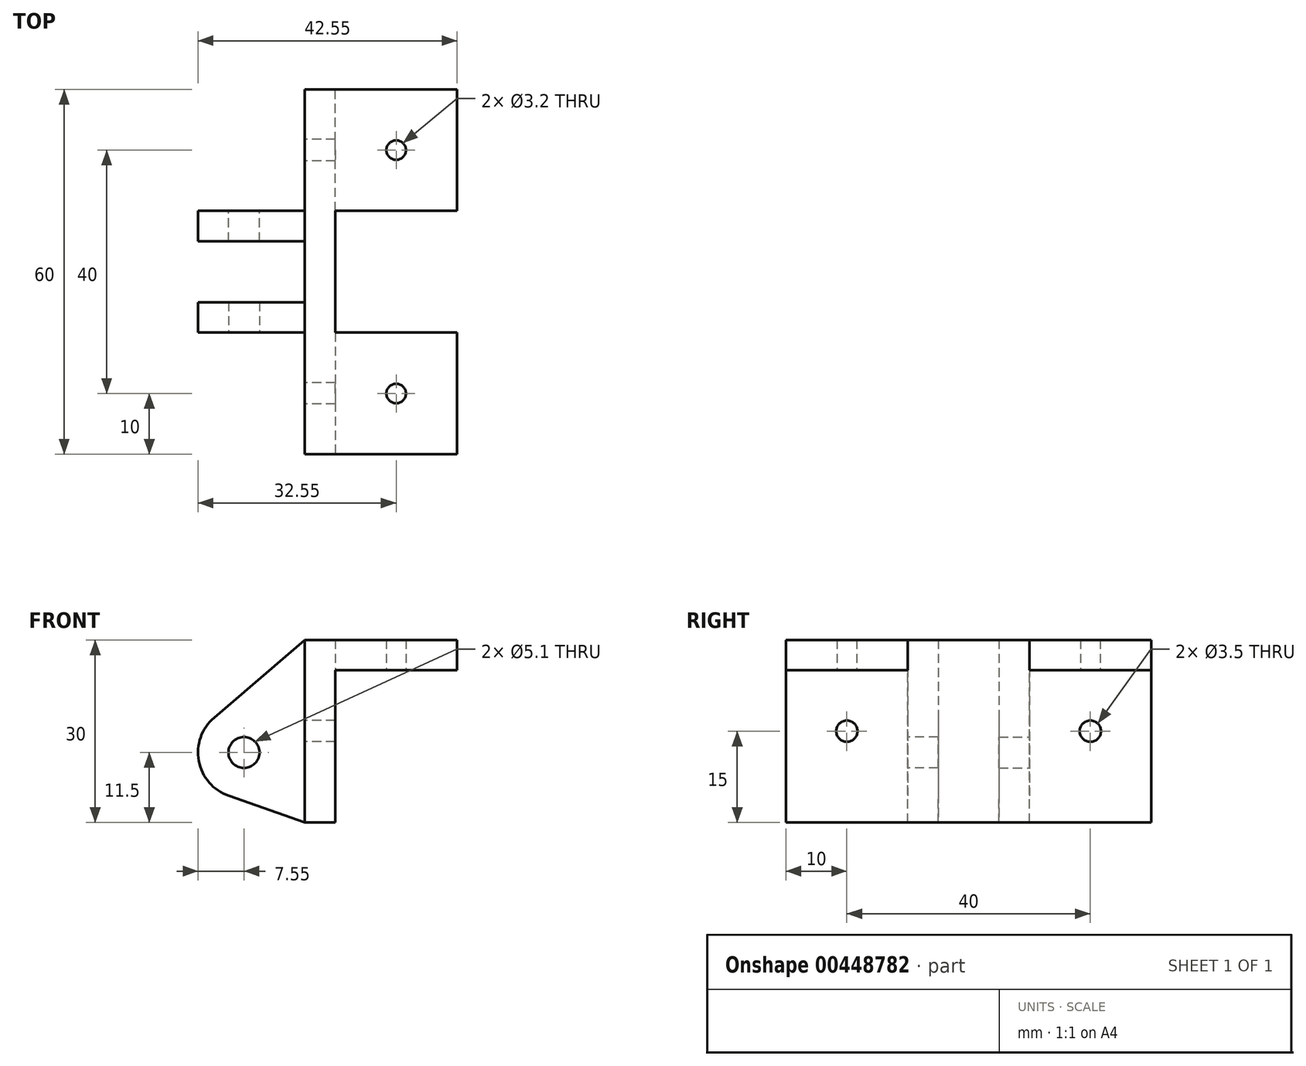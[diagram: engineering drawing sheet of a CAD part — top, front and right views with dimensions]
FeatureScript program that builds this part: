
annotation { "Feature Type Name" : "Feature", "Feature Type Description" : "" }
export const myFeature = defineFeature(function(context is Context, id is Id, definition is map)
    precondition{}
    {
        {
            var Q0;
            Q0=qCreatedBy(makeId("Front.planeOp"),FACE);
            var sketch = newSketch(context, id + "F0", { "sketchPlane" : qUnion([Q0])});
            skLineSegment(sketch, "E0", {"start": v(25, 0) * mm, "end": v(0, 0) * mm});
            skLineSegment(sketch, "E1", {"start": v(0, 0) * mm, "end": v(0, 30) * mm});
            skLineSegment(sketch, "E2", {"start": v(0, 30) * mm, "end": v(25, 30) * mm});
            skLineSegment(sketch, "E3", {"start": v(25, 30) * mm, "end": v(25, 25) * mm});
            skLineSegment(sketch, "E4", {"start": v(25, 25) * mm, "end": v(5, 25) * mm});
            skLineSegment(sketch, "E5", {"start": v(5, 25) * mm, "end": v(5, 5) * mm});
            skLineSegment(sketch, "E6", {"start": v(5, 5) * mm, "end": v(25, 5) * mm});
            skLineSegment(sketch, "E7", {"start": v(25, 5) * mm, "end": v(25, 0) * mm});
            skSolve(sketch);
        }
        {
            var Q0;
            Q0=qSketchRegion(id+"F0",true);
            extrude(context, id + "F1", {"entities" : qUnion([Q0]), "depth" : 20 * mm});
        }
        {
            var Q0;
            Q0=makeQuery(id+"F1.opExtrude","SWEPT_FACE",FACE,{"disambiguationData":[OSD([sQuery(id+"F0.wireOp",EDGE,"E4")])]});
            var sketch = newSketch(context, id + "F2", { "sketchPlane" : qUnion([Q0])});
            skPoint(sketch, "E8", {"position": v(15, 10) * mm});
            skPoint(sketch, "E8.positionSnap0", {"position": v(25, 10) * mm});
            skPoint(sketch, "E8.positionSnap1", {"position": v(15, 20) * mm});
            skSolve(sketch);
        }
        {
            var Q0;
            Q0=makeQuery(id+"F1.opExtrude","SWEPT_FACE",FACE,{"disambiguationData":[OSD([sQuery(id+"F0.wireOp",EDGE,"E6")])]});
            var sketch = newSketch(context, id + "F3", { "sketchPlane" : qUnion([Q0])});
            skPoint(sketch, "E9", {"position": v(15, -10) * mm});
            skPoint(sketch, "E9.positionSnap0", {"position": v(25, -10) * mm});
            skPoint(sketch, "E9.positionSnap1", {"position": v(15, -20) * mm});
            skSolve(sketch);
        }
        {
            var Q0;
            Q0=sQuery(id+"F2.wireOp",VERTEX,"E8");
            var Q1;
            Q1=sQuery(id+"F3.wireOp",VERTEX,"E9");
            var Q2;
            Q2=makeQuery(id+"F1.opExtrude","SWEPT_BODY",BODY,{"disambiguationData":[OSD([sQuery(id+"F0.wireOp",EDGE,"E0"),sQuery(id+"F0.wireOp",EDGE,"E1"),sQuery(id+"F0.wireOp",EDGE,"E2"),sQuery(id+"F0.wireOp",EDGE,"E3"),sQuery(id+"F0.wireOp",EDGE,"E4"),sQuery(id+"F0.wireOp",EDGE,"E5"),sQuery(id+"F0.wireOp",EDGE,"E6"),sQuery(id+"F0.wireOp",EDGE,"E7")])]});
            hole(context, id + "F4", {"style" : HoleStyle.SIMPLE, "endStyle" : HoleEndStyle.THROUGH, "holeDiameter" : 3.2 * mm, "locations" : qUnion([Q0, Q1]), "scope" : qUnion([Q2]), "isTappedThrough" : true});
        }
        {
            var Q0;
            Q0=makeQuery(id+"F1.opExtrude","CAP_FACE",FACE,{"disambiguationData":[OSD([sQuery(id+"F0.wireOp",EDGE,"E0"),sQuery(id+"F0.wireOp",EDGE,"E1"),sQuery(id+"F0.wireOp",EDGE,"E2"),sQuery(id+"F0.wireOp",EDGE,"E3"),sQuery(id+"F0.wireOp",EDGE,"E4"),sQuery(id+"F0.wireOp",EDGE,"E5"),sQuery(id+"F0.wireOp",EDGE,"E6"),sQuery(id+"F0.wireOp",EDGE,"E7")])],"isStart":false});
            var sketch = newSketch(context, id + "F5", { "sketchPlane" : qUnion([Q0])});
            skCircle(sketch, "E10", {"center": v(-10, 11.5) * mm, "radius": 2.55 * mm});
            skLineSegment(sketch, "E11", {"start": v(0, 30) * mm, "end": v(-14.91, 17.24) * mm});
            skArc(sketch, "E12.0", {"start": v(-14.91, 17.24) * mm, "mid": v(-17.42, 10.1) * mm, "end": v(-12.5, 4.37) * mm});
            skLineSegment(sketch, "E13", {"start": v(0, 0) * mm, "end": v(-12.5, 4.37) * mm});
            skLineSegment(sketch, "E14", {"start": v(0, 0) * mm, "end": v(5, 0) * mm});
            skPoint(sketch, "E14.endSnap0", {"position": v(12.5, 0) * mm});
            skLineSegment(sketch, "E15", {"start": v(5, 0) * mm, "end": v(5, 30) * mm});
            skLineSegment(sketch, "E16", {"start": v(5, 30) * mm, "end": v(0, 30) * mm});
            skSolve(sketch);
        }
        {
            var Q0;
            {var subQ4=sQuery(id+"F5.wireOp",EDGE,"E14");Q0=makeQuery(id+"F5.imprint","IMPRINT",FACE,{"disambiguationData":[TD([[makeQuery(id+"F5.imprint","IMPRINT",EDGE,{"derivedFrom":subQ4}),-1.0]])]});}
            var Q1;
            Q1=makeQuery(id+"F5.imprint","IMPRINT",FACE,{"disambiguationData":[TD([[makeQuery(id+"F5.imprint","IMPRINT",EDGE,{"derivedFrom":sQuery(id+"F5.wireOp",EDGE,"E10")}),-1.0]])]});
            extrude(context, id + "F6", {"entities" : qUnion([Q0, Q1]), "operationType" : NewBodyOperationType.ADD, "depth" : 5 * mm});
        }
        {
            var Q0;
            Q0=makeQuery(id+"F6.opExtrude","CAP_FACE",FACE,{"disambiguationData":[OSD([sQuery(id+"F5.wireOp",EDGE,"E10"),sQuery(id+"F5.wireOp",EDGE,"E11"),sQuery(id+"F5.wireOp",EDGE,"E12.0"),sQuery(id+"F5.wireOp",EDGE,"E13"),sQuery(id+"F5.wireOp",EDGE,"E14"),sQuery(id+"F5.wireOp",EDGE,"E15"),sQuery(id+"F5.wireOp",EDGE,"E16")])],"isStart":false});
            var sketch = newSketch(context, id + "F7", { "sketchPlane" : qUnion([Q0])});
            skLineSegment(sketch, "E17.bottom", {"start": v(0, 30) * mm, "end": v(5, 30) * mm});
            skLineSegment(sketch, "E17.top", {"start": v(0, 0) * mm, "end": v(5, 0) * mm});
            skLineSegment(sketch, "E17.left", {"start": v(0, 30) * mm, "end": v(0, 0) * mm});
            skLineSegment(sketch, "E17.right", {"start": v(5, 30) * mm, "end": v(5, 0) * mm});
            skSolve(sketch);
        }
        {
            var Q0;
            Q0=makeQuery(id+"F7.imprint","IMPRINT",FACE,{"disambiguationData":[TD([[makeQuery(id+"F7.imprint","IMPRINT",EDGE,{"derivedFrom":sQuery(id+"F7.wireOp",EDGE,"E17.bottom")}),-1.0]])]});
            extrude(context, id + "F8", {"entities" : qUnion([Q0]), "operationType" : NewBodyOperationType.ADD, "depth" : 5 * mm});
        }
        {
            var Q0;
            Q0=makeQuery(id+"F1.opExtrude","SWEPT_BODY",BODY,{"disambiguationData":[OSD([sQuery(id+"F0.wireOp",EDGE,"E0"),sQuery(id+"F0.wireOp",EDGE,"E1"),sQuery(id+"F0.wireOp",EDGE,"E2"),sQuery(id+"F0.wireOp",EDGE,"E3"),sQuery(id+"F0.wireOp",EDGE,"E4"),sQuery(id+"F0.wireOp",EDGE,"E5"),sQuery(id+"F0.wireOp",EDGE,"E6"),sQuery(id+"F0.wireOp",EDGE,"E7")])]});
            var Q1;
            Q1=makeQuery(id+"F8.opExtrude","CAP_FACE",FACE,{"disambiguationData":[OSD([sQuery(id+"F7.wireOp",EDGE,"E17.bottom"),sQuery(id+"F7.wireOp",EDGE,"E17.top"),sQuery(id+"F7.wireOp",EDGE,"E17.left"),sQuery(id+"F7.wireOp",EDGE,"E17.right")])],"isStart":false});
            mirror(context, id + "F9", {"operationType" : NewBodyOperationType.ADD, "entities" : qUnion([Q0]), "mirrorPlane" : qUnion([Q1])});
        }
        {
            var Q0;
            Q0=makeQuery(id+"F9.opPattern","COPY",FACE,{"derivedFrom":makeQuery(id+"F1.opExtrude","SWEPT_FACE",FACE,{"disambiguationData":[OSD([sQuery(id+"F0.wireOp",EDGE,"E6")])]}),"instanceName":"1"});
            var sketch = newSketch(context, id + "F10", { "sketchPlane" : qUnion([Q0])});
            skLineSegment(sketch, "E18.bottom", {"start": v(25, -60) * mm, "end": v(5, -60) * mm});
            skLineSegment(sketch, "E18.top", {"start": v(25, 0) * mm, "end": v(5, 0) * mm});
            skLineSegment(sketch, "E18.left", {"start": v(25, -60) * mm, "end": v(25, 0) * mm});
            skLineSegment(sketch, "E18.right", {"start": v(5, -60) * mm, "end": v(5, 0) * mm});
            skSolve(sketch);
        }
        {
            var Q0;
            {var subQ0=sQuery(id+"F10.wireOp",EDGE,"E18.top");Q0=makeQuery(id+"F10.imprint","IMPRINT",FACE,{"disambiguationData":[TD([[makeQuery(id+"F10.imprint","IMPRINT",EDGE,{"derivedFrom":subQ0}),1.0]])]});}
            var Q1;
            {var subQ2=sQuery(id+"F10.wireOp",EDGE,"E18.bottom");Q1=makeQuery(id+"F10.imprint","IMPRINT",FACE,{"disambiguationData":[TD([[makeQuery(id+"F10.imprint","IMPRINT",EDGE,{"derivedFrom":subQ2}),1.0]])]});}
            var Q2;
            {var subQ0=makeQuery(id+"F8.boolean.opBoolean","MERGE",FACE,{"derivedFrom":[makeQuery(id+"F6.boolean.opBoolean","MERGE",FACE,{"derivedFrom":[makeQuery(id+"F1.opExtrude","SWEPT_FACE",FACE,{"disambiguationData":[OSD([sQuery(id+"F0.wireOp",EDGE,"E0")])]}),makeQuery(id+"F6.opExtrude","SWEPT_FACE",FACE,{"disambiguationData":[OSD([sQuery(id+"F5.wireOp",EDGE,"E14")])]})]}),makeQuery(id+"F8.opExtrude","SWEPT_FACE",FACE,{"disambiguationData":[OSD([sQuery(id+"F7.wireOp",EDGE,"E17.top")])]})]});Q2=makeQuery(id+"F9.boolean.opBoolean","MERGE",FACE,{"derivedFrom":[subQ0,makeQuery(id+"F9.opPattern","COPY",FACE,{"derivedFrom":subQ0,"instanceName":"1"})]});}
            extrude(context, id + "F11", {"entities" : qUnion([Q0, Q1]), "operationType" : NewBodyOperationType.REMOVE, "endBound" : BoundingType.UP_TO_SURFACE, "oppositeDirection" : true, "endBoundEntityFace" : qUnion([Q2]), "depth" : 25 * mm});
        }
        {
            var Q0;
            Q0=makeQuery(id+"F1.opExtrude","SWEPT_FACE",FACE,{"disambiguationData":[OSD([sQuery(id+"F0.wireOp",EDGE,"E1")])]});
            var sketch = newSketch(context, id + "F12", { "sketchPlane" : qUnion([Q0])});
            skPoint(sketch, "E19", {"position": v(10, 15) * mm});
            skPoint(sketch, "E20", {"position": v(50, 15) * mm});
            skSolve(sketch);
        }
        {
            var Q0;
            Q0=sQuery(id+"F12.wireOp",VERTEX,"E19");
            var Q1;
            Q1=sQuery(id+"F12.wireOp",VERTEX,"E20");
            var Q2;
            Q2=makeQuery(id+"F1.opExtrude","SWEPT_BODY",BODY,{"disambiguationData":[OSD([sQuery(id+"F0.wireOp",EDGE,"E0"),sQuery(id+"F0.wireOp",EDGE,"E1"),sQuery(id+"F0.wireOp",EDGE,"E2"),sQuery(id+"F0.wireOp",EDGE,"E3"),sQuery(id+"F0.wireOp",EDGE,"E4"),sQuery(id+"F0.wireOp",EDGE,"E5"),sQuery(id+"F0.wireOp",EDGE,"E6"),sQuery(id+"F0.wireOp",EDGE,"E7")])]});
            hole(context, id + "F13", {"style" : HoleStyle.SIMPLE, "endStyle" : HoleEndStyle.BLIND, "holeDiameter" : 3.5 * mm, "holeDepth" : 10 * mm, "tappedDepth" : 12 * mm, "tapClearance" : 3, "locations" : qUnion([Q0, Q1]), "scope" : qUnion([Q2])});
        }
    });
